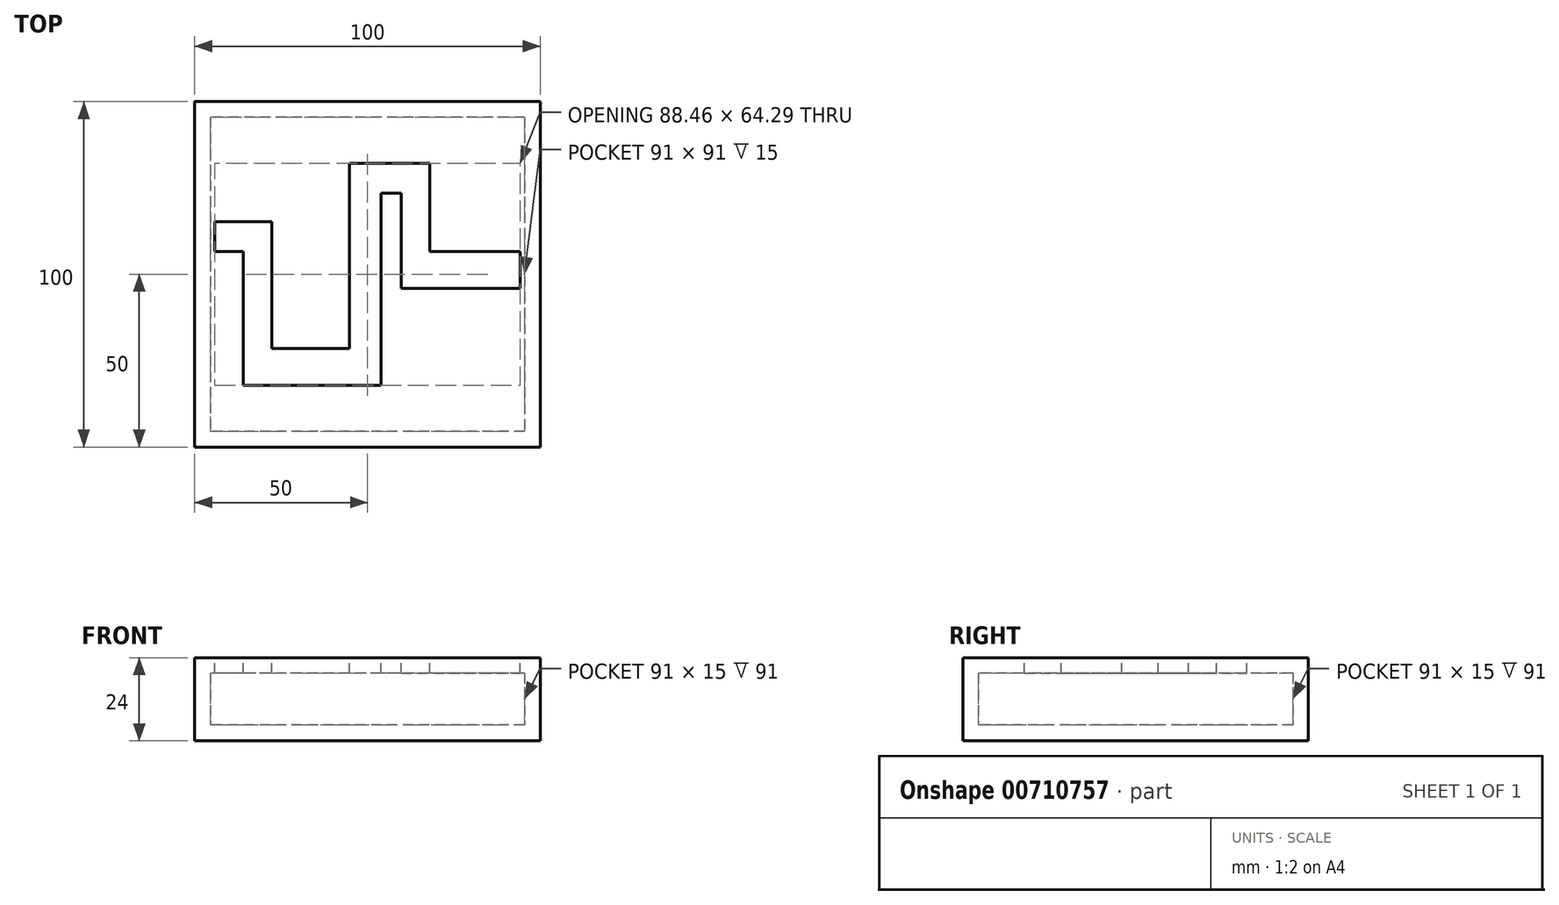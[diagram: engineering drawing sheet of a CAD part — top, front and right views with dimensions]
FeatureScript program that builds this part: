
annotation { "Feature Type Name" : "Feature", "Feature Type Description" : "" }
export const myFeature = defineFeature(function(context is Context, id is Id, definition is map)
    precondition{}
    {
        {
            var Q0;
            Q0=qCreatedBy(makeId("Top.planeOp"),FACE);
            var sketch = newSketch(context, id + "F0", { "sketchPlane" : qUnion([Q0])});
            skLineSegment(sketch, "E0.bottom", {"start": v(50, 50) * mm, "end": v(-50, 50) * mm});
            skLineSegment(sketch, "E0.top", {"start": v(50, -50) * mm, "end": v(-50, -50) * mm});
            skLineSegment(sketch, "E0.left", {"start": v(50, 50) * mm, "end": v(50, -50) * mm});
            skLineSegment(sketch, "E0.right", {"start": v(-50, 50) * mm, "end": v(-50, -50) * mm});
            skPoint(sketch, "E0.middle", {"position": v(0, 0) * mm});
            skSolve(sketch);
        }
        {
            var Q0;
            Q0=makeQuery(id+"F0.imprint","IMPRINT",FACE,{"disambiguationData":[TD([[makeQuery(id+"F0.imprint","IMPRINT",EDGE,{"derivedFrom":sQuery(id+"F0.wireOp",EDGE,"E0.bottom")}),1.0]])]});
            extrude(context, id + "F1", {"entities" : qUnion([Q0]), "depth" : 4.5 * mm, "offsetDistance" : 25 * mm});
        }
        {
            var Q0;
            Q0=makeQuery(id+"F1.opExtrude","CAP_FACE",FACE,{"disambiguationData":[OSD([sQuery(id+"F0.wireOp",EDGE,"E0.bottom"),sQuery(id+"F0.wireOp",EDGE,"E0.top"),sQuery(id+"F0.wireOp",EDGE,"E0.left"),sQuery(id+"F0.wireOp",EDGE,"E0.right")])],"isStart":false});
            var sketch = newSketch(context, id + "F2", { "sketchPlane" : qUnion([Q0])});
            skLineSegment(sketch, "E1.bottom", {"start": v(50, 50) * mm, "end": v(-50, 50) * mm});
            skLineSegment(sketch, "E1.top", {"start": v(50, -50) * mm, "end": v(-50, -50) * mm});
            skLineSegment(sketch, "E1.left", {"start": v(50, 50) * mm, "end": v(50, -50) * mm});
            skLineSegment(sketch, "E1.right", {"start": v(-50, 50) * mm, "end": v(-50, -50) * mm});
            skPoint(sketch, "E1.middle", {"position": v(0, 0) * mm});
            skLineSegment(sketch, "E2.0", {"start": v(45.5, 45.5) * mm, "end": v(-45.5, 45.5) * mm});
            skLineSegment(sketch, "E2.1", {"start": v(45.5, 45.5) * mm, "end": v(45.5, -45.5) * mm});
            skLineSegment(sketch, "E2.2", {"start": v(45.5, -45.5) * mm, "end": v(-45.5, -45.5) * mm});
            skLineSegment(sketch, "E2.3", {"start": v(-45.5, 45.5) * mm, "end": v(-45.5, -45.5) * mm});
            skSolve(sketch);
        }
        {
            var Q0;
            Q0 = qSketchRegion(id + "F2", true);
            extrude(context, id + "F3", {"entities" : qUnion([Q0]), "operationType" : NewBodyOperationType.ADD, "depth" : 15 * mm, "offsetDistance" : 25 * mm});
        }
        {
            var Q0;
            Q0=makeQuery(id+"F3.opExtrude","CAP_FACE",FACE,{"disambiguationData":[OSD([sQuery(id+"F2.wireOp",EDGE,"E1.bottom"),sQuery(id+"F2.wireOp",EDGE,"E1.top"),sQuery(id+"F2.wireOp",EDGE,"E1.left"),sQuery(id+"F2.wireOp",EDGE,"E1.right"),sQuery(id+"F2.wireOp",EDGE,"E2.0"),sQuery(id+"F2.wireOp",EDGE,"E2.1"),sQuery(id+"F2.wireOp",EDGE,"E2.2"),sQuery(id+"F2.wireOp",EDGE,"E2.3")])],"isStart":false});
            var sketch = newSketch(context, id + "F4", { "sketchPlane" : qUnion([Q0])});
            skLineSegment(sketch, "E3.bottom", {"start": v(50, 50) * mm, "end": v(-50, 50) * mm});
            skLineSegment(sketch, "E3.top", {"start": v(50, -50) * mm, "end": v(-50, -50) * mm});
            skLineSegment(sketch, "E3.left", {"start": v(50, 50) * mm, "end": v(50, -50) * mm});
            skLineSegment(sketch, "E3.right", {"start": v(-50, 50) * mm, "end": v(-50, -50) * mm});
            skPoint(sketch, "E3.middle", {"position": v(0, 0) * mm});
            skSolve(sketch);
        }
        {
            var Q0;
            Q0 = qSketchRegion(id + "F4", true);
            extrude(context, id + "F5", {"entities" : qUnion([Q0]), "operationType" : NewBodyOperationType.ADD, "depth" : 4.5 * mm, "offsetDistance" : 25 * mm});
        }
        {
            var Q0;
            Q0=makeQuery(id+"F5.opExtrude","CAP_FACE",FACE,{"disambiguationData":[OSD([sQuery(id+"F4.wireOp",EDGE,"E3.bottom"),sQuery(id+"F4.wireOp",EDGE,"E3.top"),sQuery(id+"F4.wireOp",EDGE,"E3.left"),sQuery(id+"F4.wireOp",EDGE,"E3.right")])],"isStart":false});
            var sketch = newSketch(context, id + "F6", { "sketchPlane" : qUnion([Q0])});
            skLineSegment(sketch, "E4", {"start": v(44.23, 6.57) * mm, "end": v(18.08, 6.57) * mm});
            skLineSegment(sketch, "E5", {"start": v(18.08, 6.57) * mm, "end": v(18.08, 32.14) * mm});
            skPoint(sketch, "E6.end.orphan", {"position": v(0, 34.07) * mm});
            skLineSegment(sketch, "E7", {"start": v(18.08, 32.14) * mm, "end": v(-5.23, 32.14) * mm});
            skLineSegment(sketch, "E8", {"start": v(-5.23, 32.14) * mm, "end": v(-5.23, -21.52) * mm});
            skLineSegment(sketch, "E9", {"start": v(-5.23, -21.52) * mm, "end": v(-27.64, -21.52) * mm});
            skLineSegment(sketch, "E10", {"start": v(-27.64, -21.52) * mm, "end": v(-27.64, 15.24) * mm});
            skLineSegment(sketch, "E11", {"start": v(-27.64, 15.24) * mm, "end": v(-44.23, 15.24) * mm});
            skLineSegment(sketch, "E12.0", {"start": v(-35.9, 6.54) * mm, "end": v(-44.23, 6.54) * mm});
            skLineSegment(sketch, "E12.1", {"start": v(-35.9, -32.14) * mm, "end": v(-35.9, 6.54) * mm});
            skLineSegment(sketch, "E12.2", {"start": v(3.92, -32.14) * mm, "end": v(-35.9, -32.14) * mm});
            skLineSegment(sketch, "E12.4", {"start": v(9.83, -4.05) * mm, "end": v(9.83, 23.44) * mm});
            skLineSegment(sketch, "E12.5", {"start": v(9.83, 23.44) * mm, "end": v(3.92, 23.44) * mm});
            skLineSegment(sketch, "E12.6", {"start": v(3.92, 23.44) * mm, "end": v(3.92, -32.14) * mm});
            skLineSegment(sketch, "E13", {"start": v(44.23, -2.13) * mm, "end": v(44.23, 6.57) * mm});
            skPoint(sketch, "E13.endSnap0", {"position": v(34.04, 6.57) * mm});
            skLineSegment(sketch, "E14", {"start": v(-44.23, 15.24) * mm, "end": v(-44.23, 6.54) * mm});
            skPoint(sketch, "E15.orphan", {"position": v(50, 6.57) * mm});
            skPoint(sketch, "E16.end.orphan", {"position": v(-50, 15.24) * mm});
            skPoint(sketch, "E17.start.orphan", {"position": v(6.43, 32.14) * mm});
            skLineSegment(sketch, "E18", {"start": v(9.83, -4.05) * mm, "end": v(44.23, -4.05) * mm});
            skLineSegment(sketch, "E19", {"start": v(44.23, -4.05) * mm, "end": v(44.23, 6.57) * mm});
            skSolve(sketch);
        }
        {
            var Q0;
            Q0 = qSketchRegion(id + "F6", true);
            extrude(context, id + "F7", {"entities" : qUnion([Q0]), "operationType" : NewBodyOperationType.REMOVE, "oppositeDirection" : true, "depth" : 6 * mm, "offsetDistance" : 25 * mm});
        }
    });
